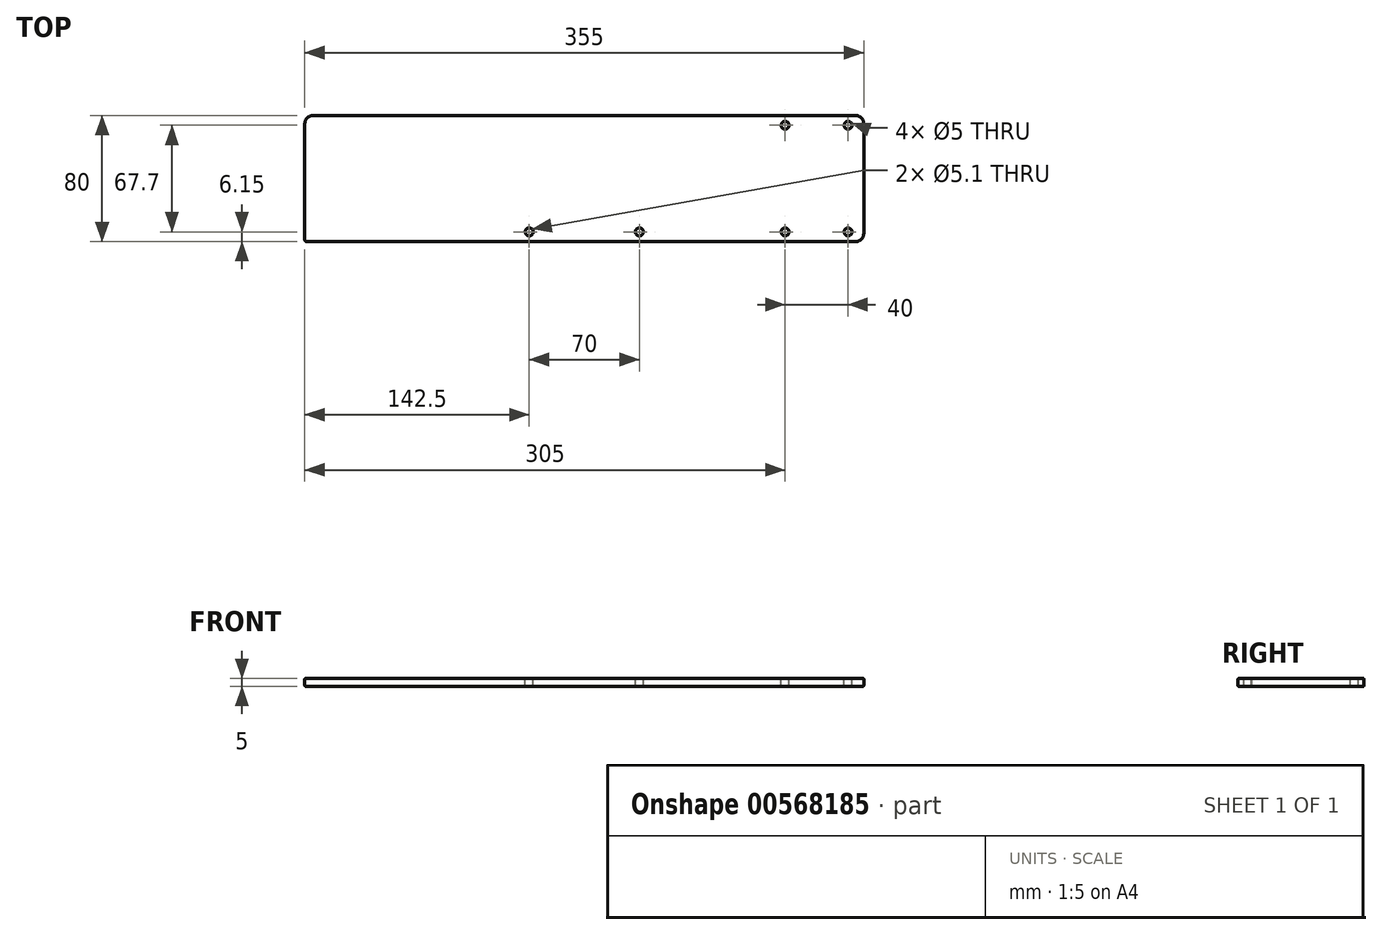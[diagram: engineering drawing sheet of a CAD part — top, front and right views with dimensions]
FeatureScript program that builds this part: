
annotation { "Feature Type Name" : "Feature", "Feature Type Description" : "" }
export const myFeature = defineFeature(function(context is Context, id is Id, definition is map)
    precondition{}
    {
        {
            var Q0;
            Q0=qCreatedBy(makeId("Top.planeOp"),FACE);
            var sketch = newSketch(context, id + "F0", { "sketchPlane" : qUnion([Q0])});
            skLineSegment(sketch, "E0.bottom", {"start": v(1, 0) * mm, "end": v(350, 0) * mm});
            skLineSegment(sketch, "E0.top", {"start": v(5, 80) * mm, "end": v(350, 80) * mm});
            skLineSegment(sketch, "E0.left", {"start": v(0, 1) * mm, "end": v(0, 75) * mm});
            skLineSegment(sketch, "E0.right", {"start": v(355, 5) * mm, "end": v(355, 75) * mm});
            skPoint(sketch, "E1.visualSharp", {"position": v(0, 80) * mm});
            skArc(sketch, "E1.filletArc", {"start": v(5, 80) * mm, "mid": v(1.46, 78.54) * mm, "end": v(0, 75) * mm});
            skPoint(sketch, "E2.visualSharp", {"position": v(355, 80) * mm});
            skArc(sketch, "E2.filletArc", {"start": v(355, 75) * mm, "mid": v(353.54, 78.54) * mm, "end": v(350, 80) * mm});
            skPoint(sketch, "E3.visualSharp", {"position": v(355, 0) * mm});
            skArc(sketch, "E3.filletArc", {"start": v(350, 0) * mm, "mid": v(353.54, 1.46) * mm, "end": v(355, 5) * mm});
            skPoint(sketch, "E4.visualSharp", {"position": v(0, 0) * mm});
            skArc(sketch, "E4.filletArc", {"start": v(0, 1) * mm, "mid": v(0.3, 0.3) * mm, "end": v(1, 0) * mm});
            skSolve(sketch);
        }
        {
            var Q0;
            Q0=makeQuery(id+"F0.imprint","IMPRINT",FACE,{"disambiguationData":[TD([[makeQuery(id+"F0.imprint","IMPRINT",EDGE,{"derivedFrom":sQuery(id+"F0.wireOp",EDGE,"E0.bottom")}),1.0]])]});
            extrude(context, id + "F1", {"entities" : qUnion([Q0]), "depth" : 5 * mm, "offsetDistance" : 25 * mm});
        }
        {
            var Q0;
            Q0=makeQuery(id+"F1.opExtrude","CAP_FACE",FACE,{"disambiguationData":[OSD([sQuery(id+"F0.wireOp",EDGE,"E0.bottom"),sQuery(id+"F0.wireOp",EDGE,"E0.top"),sQuery(id+"F0.wireOp",EDGE,"E0.left"),sQuery(id+"F0.wireOp",EDGE,"E0.right"),sQuery(id+"F0.wireOp",EDGE,"E1.filletArc"),sQuery(id+"F0.wireOp",EDGE,"E2.filletArc"),sQuery(id+"F0.wireOp",EDGE,"E3.filletArc"),sQuery(id+"F0.wireOp",EDGE,"E4.filletArc")])],"isStart":false});
            var Q1;
            Q1=makeQuery(id+"F1.opExtrude","CAP_FACE",FACE,{"disambiguationData":[OSD([sQuery(id+"F0.wireOp",EDGE,"E0.bottom"),sQuery(id+"F0.wireOp",EDGE,"E0.top"),sQuery(id+"F0.wireOp",EDGE,"E0.left"),sQuery(id+"F0.wireOp",EDGE,"E0.right"),sQuery(id+"F0.wireOp",EDGE,"E1.filletArc"),sQuery(id+"F0.wireOp",EDGE,"E2.filletArc"),sQuery(id+"F0.wireOp",EDGE,"E3.filletArc"),sQuery(id+"F0.wireOp",EDGE,"E4.filletArc")])],"isStart":true});
            fillet(context, id + "F2", {"entities" : qUnion([Q0, Q1]), "radius" : 0.5 * mm, "tangentPropagation" : true, "allowEdgeOverflow" : false});
        }
        {
            var Q0;
            Q0=makeQuery(id+"F1.opExtrude","CAP_FACE",FACE,{"disambiguationData":[OSD([sQuery(id+"F0.wireOp",EDGE,"E0.bottom"),sQuery(id+"F0.wireOp",EDGE,"E0.top"),sQuery(id+"F0.wireOp",EDGE,"E0.left"),sQuery(id+"F0.wireOp",EDGE,"E0.right"),sQuery(id+"F0.wireOp",EDGE,"E1.filletArc"),sQuery(id+"F0.wireOp",EDGE,"E2.filletArc"),sQuery(id+"F0.wireOp",EDGE,"E3.filletArc"),sQuery(id+"F0.wireOp",EDGE,"E4.filletArc")])],"isStart":false});
            var sketch = newSketch(context, id + "F3", { "sketchPlane" : qUnion([Q0])});
            skCircle(sketch, "E5", {"center": v(345, 73.85) * mm, "radius": 2.5 * mm});
            skCircle(sketch, "E6.0.1.0", {"center": v(345, 6.15) * mm, "radius": 2.5 * mm});
            skCircle(sketch, "E6.1.0.0", {"center": v(305, 73.85) * mm, "radius": 2.5 * mm});
            skCircle(sketch, "E6.1.1.0", {"center": v(305, 6.15) * mm, "radius": 2.5 * mm});
            skLineSegment(sketch, "E6.direction1", {"start": v(345, 73.85) * mm, "end": v(305, 73.85) * mm, "construction": true});
            skLineSegment(sketch, "E6.direction2", {"start": v(345, 73.85) * mm, "end": v(345, 6.15) * mm, "construction": true});
            skSolve(sketch);
        }
        {
            var Q0;
            Q0 = qSketchRegion(id + "F3", true);
            extrude(context, id + "F4", {"entities" : qUnion([Q0]), "operationType" : NewBodyOperationType.REMOVE, "oppositeDirection" : true, "depth" : 25 * mm, "offsetDistance" : 25 * mm});
        }
        {
            var Q0;
            Q0=makeQuery(id+"F1.opExtrude","CAP_FACE",FACE,{"disambiguationData":[OSD([sQuery(id+"F0.wireOp",EDGE,"E0.bottom"),sQuery(id+"F0.wireOp",EDGE,"E0.top"),sQuery(id+"F0.wireOp",EDGE,"E0.left"),sQuery(id+"F0.wireOp",EDGE,"E0.right"),sQuery(id+"F0.wireOp",EDGE,"E1.filletArc"),sQuery(id+"F0.wireOp",EDGE,"E2.filletArc"),sQuery(id+"F0.wireOp",EDGE,"E3.filletArc"),sQuery(id+"F0.wireOp",EDGE,"E4.filletArc")])],"isStart":false});
            var sketch = newSketch(context, id + "F5", { "sketchPlane" : qUnion([Q0])});
            skCircle(sketch, "E7", {"center": v(142.5, 6.15) * mm, "radius": 2.55 * mm});
            skCircle(sketch, "E8", {"center": v(212.5, 6.15) * mm, "radius": 2.55 * mm});
            skLineSegment(sketch, "E9", {"start": v(177.5, 0) * mm, "end": v(177.5, 79.5) * mm, "construction": true});
            skPoint(sketch, "E9.startSnap0", {"position": v(177.5, 6.15) * mm});
            skSolve(sketch);
        }
        {
            var Q0;
            Q0 = qSketchRegion(id + "F5", true);
            extrude(context, id + "F6", {"entities" : qUnion([Q0]), "operationType" : NewBodyOperationType.REMOVE, "oppositeDirection" : true, "depth" : 25 * mm, "offsetDistance" : 25 * mm});
        }
    });
